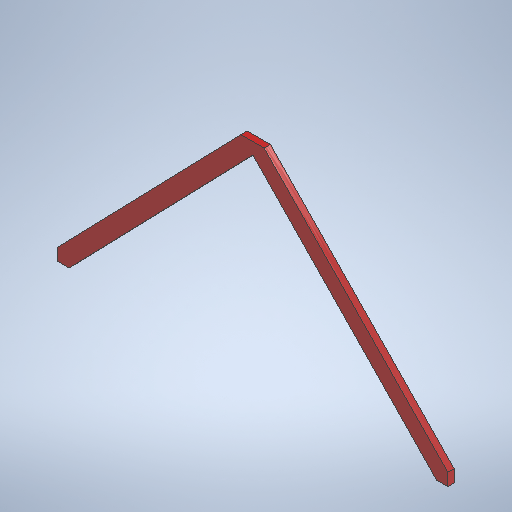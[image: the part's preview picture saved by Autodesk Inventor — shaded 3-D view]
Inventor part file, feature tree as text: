
AUTODESK INVENTOR PART (.ipt)
format: ipt  version: 2025.1 (Build 291241020, 241B)  size: 262,656 bytes
history: native  units: in
note: dims shown in document units (in); Inventor stores cm internally (conversion verified against a paired STEP export)
features: other x7, reference x4, extrude x1, sketch x1
ambient origin geometry x8: Origin, YZ Plane, XZ Plane, XY Plane, X Axis, Y Axis, Z Axis, Center Point
bodies: Solid1 (feature_tree)
feature tree (13):
  extrude  "Extrusion1"  [1 undecoded]
  sketch  "Sketch1"  dims[d0=1.5in d1=0.0in]
  reference  "Reference1"
  reference  "Reference2"
  reference  "Reference3"
  reference  "Reference4"
  other  "<userpath>\Documents\Tburn24\B_Legs0\B_Legs0.iam"
  other  "B_Legs0.iam"
  other  "8'x2x4:4"
  other  "4x2x4:3"
  other  "8'x2x4:2"
  other  "4x2x4:2"
  other  "Finish1"
note: 1 required parameter value undecoded (feature->parameter linkage not recoverable at this tier; creation-order binding heuristic only, values carry confidence <= 0.55)
